# Revit family: 50617183
name_source: partatom
category: Plumbing Fixtures
revit_build: Autodesk Revit 2016 (Build: 20150714_1515(x64)
units: mm (PartAtom-declared; Revit-internal decimal feet)

## family parameters
Always vertical = Yes
Cut with Voids When Loaded = No
OmniClass Number = 23.45.55.00
OmniClass Title = Sanitary Faucets, Wastes
Part Type = Normal
Room Calculation Point = No
Round Connector Dimension = Use Diameter
Shared = No
Work Plane-Based = No

## types (1)
- 50617183 Cover part for shower faucet
    Approval ACS = 16 ACC NY 205
    AssetType = Fixed
    BIMObjectName = 50617183
    BodyMaterial = Brass
    Brand = Hansa
    Catalog Drawing URL = http://static.hansa.com
    Category = Bathroom, shower
    Class = Single lever, trim kit
    CloseOffRating = 0
    Color = Chrome
    ConvergoRefNr = 0087-1803-0078-FI
    Customs Code = 84819000
    Dimension Drawing URL = http://static.hansa.com
    DurationUnit = Year
    EAN Number = 4057304008597
    FDV Document URL = http://www.hansa.com
    FaucetMainMaterial = Brass
    Features = Single lever, trim kit
    Finish = Polished
    Flow Drawing URL = http://static.hansa.com
    Flow Rate At 300kPa = 0.3 L/s
    FlowCoefficient = 0
    Group = Shower faucets
    IfcExportAs = IfcValveType
    IfcExportType = FAUCET
    Installation Type = Wall mounted for concealed unit
    Installation and Maintenance = http://static.hansa.com
    ManufacterURL = http://www.hansa.com
    Manufacturer = Hansa
    ManufacturerName = Hansa
    Market = BEL;CZE;ESP;INT;ITA;SVK
    Material = Brass
    Model = 50617183 Cover part for shower faucet
    ModelReference = 50617183
    NBSDescription = Water supply fittings for baths
    NBSReference = 45-35-70/315
    Name = 50617183 Cover part for shower faucet
    Name_en = 50617183 Cover part for shower faucet
    NominalDepth = 102 mm
    NominalHeight = 175 mm  [stored 0.574147 ft]
    NominalWidth = 120 mm  [stored 0.393701 ft]
    Package external Dimensions = 210 x 208 x 85
    Product Code = 50617183
    Product Datasheet = http://www.hansa.com
    Product Family = HANSAPOLO
    Product Image URL = http://static.hansa.com
    Product URL = http://static.hansa.com
    Shape = Sculptured
    Size = 120x102x175 mm
    URL ACS = http://static.hansa.com
    Uniclass2 = Pr_40_30_96_78
    Uniclass2015Description = Shower manual water supply sets
    Uniclass2015Reference = Pr_40_20_87_78
    Version = 1
    VersionDate = 21/03/2019
    WarrantyDescription = http://warranty.hansa.com
    WarrantyDurationUnit = Year

note: [stored X ft] marks values corroborated as IEEE doubles in the binary element streams (Revit-internal decimal feet)

## geometry (parser evidence)
native form markers: Sweep x6
no freeform markers — native parametric forms only
